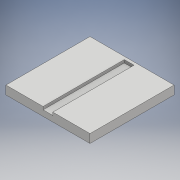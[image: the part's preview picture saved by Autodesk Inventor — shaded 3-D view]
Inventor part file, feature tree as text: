
AUTODESK INVENTOR PART (.ipt)
format: ipt  version: 2018.3 (Build 223284000, 284)  size: 112,640 bytes
history: native  units: mm
features: extrude x3, sketch x3
ambient origin geometry x8: Origin, YZ Plane, XZ Plane, XY Plane, X Axis, Y Axis, Z Axis, Center Point
bodies: Solid1 (feature_tree)
feature tree (6):
  extrude  "Extrusion1"  Depth=14.7mm
  extrude  "Extrusion2"  Depth=0.5mm TaperAngle=0.0deg
  extrude  "Extrusion3"  Depth=6.5mm
  sketch  "Sketch1"  dims[d0=14.7mm d1=14.7mm]
  sketch  "Sketch2"  dims[d2=1.5mm d3=0.0mm d4=0.5mm d5=0.0mm]
  sketch  "Sketch3"  dims[d6=1.7mm d7=6.5mm d8=0.5mm d9=0.5mm d10=0.0mm]
